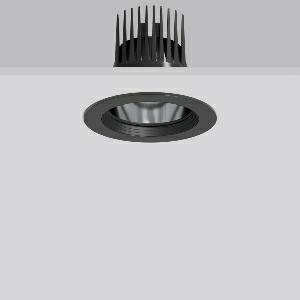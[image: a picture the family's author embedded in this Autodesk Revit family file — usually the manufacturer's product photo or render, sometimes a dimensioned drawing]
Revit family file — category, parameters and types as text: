
# Revit family: heledon_maxi_e_901770_003_da21
name_source: partatom
category: Lighting Fixtures
units: mm (PartAtom-declared; Revit-internal decimal feet)

## family parameters
Cut with Voids When Loaded = No
Host = Face
Light Source = No
Part Type = Normal
Room Calculation Point = No
Round Connector Dimension = Use Diameter
Shared = No

## types (1)
- HELEDON maxi E (1 x LED Modul 932 fresh meat, 2100 lm, 3200)
    Apparent Load = 33 VA
    Approval mark = CE
    CIE Flux Codes = 100 100 100 100 100
    Color Rendering = 90
    Color Temperature = 3200
    Default Elevation = 1800 mm
    Description = Series: HELEDON maxi
Round recessed downlight. Housing: die-cast aluminium, powder-coated. Black plastic ring and recessed LED to prevent glare from the side. Optical assembly with reflector made of MIRO-Silver with 98% total light reflection for outstanding efficiency - can be changed without tools. Special LED for illumination of meat included. Suitable for Recessed ceiling mounting. Installation without tools thanks to spring fastening system. Including separate LED converter with connecting cable 600 mm.High quality converter without flickering and stroboscopic effect. Through-wiring box (5 pole) available as accessory. The following accessories can be mounted without use of tools: interchangeable lenses, decorative glasses, honeycomb louvre, clear and frosted diffusers, white interchangeable plastic ring. 
Colour: deep black, matt (RAL 9005)
Diameter: 162 mm
Height: 3 mm
Cut-out diameter: 152 mm
Recess height: 200 mm
Luminaire: recess height: 135 mm
Lamp: LED
Socket: without socket
Colour temperature: fresh meat
System power: 33 W
Rated luminous flux: 2100 lm
Luminous efficiency: 64 lm/W
Control gear: Regulated power supply
Protection class: II
Type of protection: IP 20
    Height = 0 mm  [stored 0 ft]
    Lamp = 1 x LED Modul 932 fresh meat
    Lamp Light Flux = 2100 lm
    Lamp count = 1
    Length = 162 mm
    Lifetime = 50000 h
    Luminous efficacy = 64 lm/W
    Manufacturer = RZB
    ModVariant = No
    Model = 901770.003
    Mounting Place = Ceiling
    Mounting Type = Recessed
    Number of Poles = 1
    OnlyDefault = Yes
    Power Factor = 1
    Product Name = HELEDON maxi E
    Product group = Recessed downlights
    ProductGroupID = 402
    Protection Class = Protection class II
    Protection Degree = IP 20
    RLX_Detail_Level = 1
    RLX_Emergency_Light_Flux = 0 lm
    RLX_Emergency_Type = 0
    RLX_Emergency_Type_DB = No
    RlxData = <blob elided: 122029 chars, md5=c621670e>
    Socket = socket
    Standby Power = 0 W
    System Light Flux = 2100 lm
    System Power = 33 W
    Type Comments = Product without accessories
    Type Image = 901662.003.jpg
    URL = http://relux.com
    VarID = ---
    Voltage = 230 V
    Voltage Range = 220-240 V
    Weight = 0.00 kg
    Width = 0 mm  [stored 0 ft]

note: [stored X ft] marks values corroborated as IEEE doubles in the binary element streams (Revit-internal decimal feet)

## geometry (parser evidence)
native form markers: Blend x4, Sweep x12
no freeform markers — native parametric forms only
